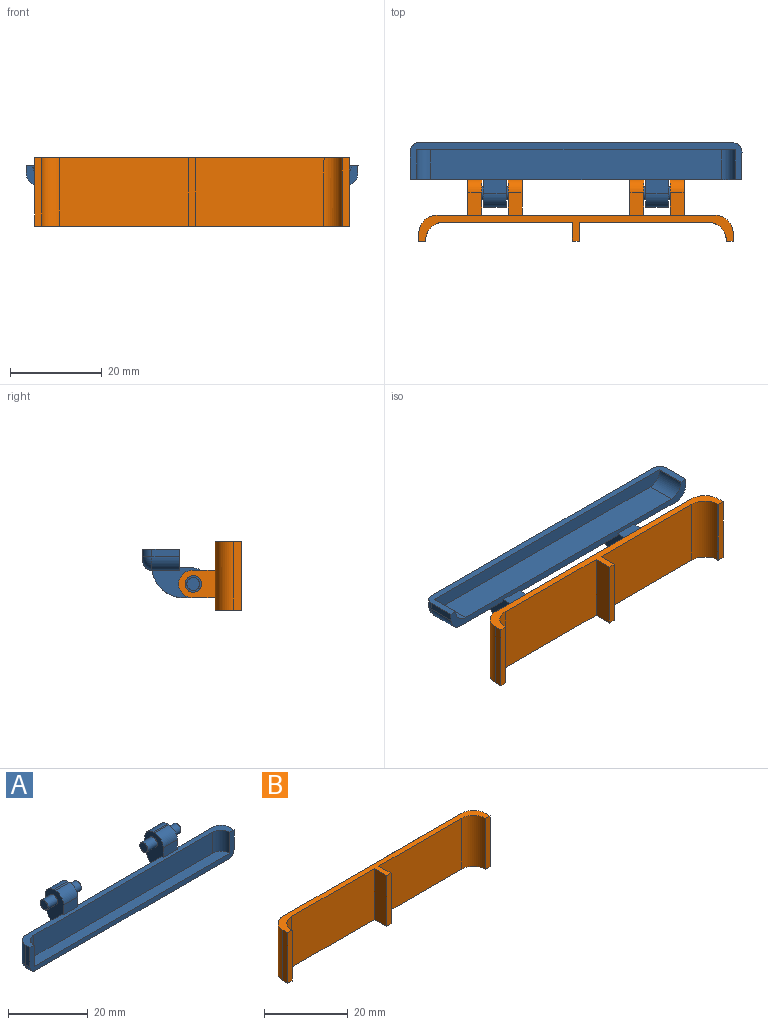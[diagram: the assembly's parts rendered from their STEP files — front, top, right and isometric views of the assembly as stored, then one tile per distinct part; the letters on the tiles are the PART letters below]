
ASSEMBLY  parts=2 mates=1
PART A: 45 faces, bbox 72.3x10.6x14 mm
  f0: plane 72.3x4.58mm, normal (0,0,1), area 112.7mm2, adj f2,f3,f4,f5,f9,f10,f11,f12
  f1: plane 68.3x2.58mm, normal (0,0,-1), area 175.9mm2, adj f7,f8,f17,f18,f19,f44
  f2: plane 6x1.58mm, normal (-1,0,0), area 9.5mm2, adj f0,f8,f12,f44
  f3: plane 6x1.58mm, normal (1,0,0), area 9.5mm2, adj f0,f7,f13,f44
  f4: plane 6.5x0.08mm, normal (-1,0,0), area 0.5mm2, adj f0,f6,f14,f44
  f5: plane 6.5x0.08mm, normal (1,0,0), area 0.5mm2, adj f0,f6,f16,f44
  f6: plane 69.3x3.08mm, normal (0,0,1), area 209.7mm2, adj f4,f5,f14,f15,f16,f44
  f7: cylinder r=2mm len=2mm, axis (0,-1,0), area 5mm2, adj f1,f3,f17,f44
  f8: cylinder r=2mm len=2mm, axis (0,1,0), area 5mm2, adj f1,f2,f18,f44
  f9: plane 13x6mm, normal (0,1,0), area 78mm2, adj f0,f13,f19,f26
  f10: plane 30.3x6mm, normal (0,1,0), area 181.8mm2, adj f0,f19,f22,f28
  f11: plane 13x6mm, normal (0,1,0), area 78mm2, adj f0,f12,f19,f20
  f12: cylinder r=3mm len=6mm, axis (0,0,1), area 28.3mm2, adj f0,f2,f11,f18
  f13: cylinder r=3mm len=6mm, axis (0,0,1), area 28.3mm2, adj f0,f3,f9,f17
  f14: cylinder r=3mm len=6.5mm, axis (0,0,1), area 30.6mm2, adj f0,f4,f6,f15
  f15: plane 63.3x6.5mm, normal (0,-1,0), area 411.4mm2, adj f0,f6,f14,f16
  f16: cylinder r=3mm len=6.5mm, axis (0,0,1), area 30.6mm2, adj f0,f5,f6,f15
  f17: torus R=1mm, axis (0,0,1), area 11.2mm2, adj f1,f7,f13,f19
  f18: torus R=1mm, axis (0,0,1), area 11.2mm2, adj f1,f8,f12,f19
  f19: cylinder r=2mm len=66.3mm, axis (1,0,0), area 208.3mm2, adj f1,f9,f10,f11,f17,f18,f42,f43
  f20: plane 12x6.5mm, normal (-1,0,0), area 54.9mm2, adj f0,f11,f21,f23,f24,f32,f33,f34
  f21: plane 5x3mm, normal (0,-1,0), area 15mm2, adj f0,f20,f22,f33
  f22: plane 12x6.5mm, normal (1,0,0), area 54.9mm2, adj f0,f10,f21,f23,f24,f32,f33,f36
  f23: plane 5x2.07mm, normal (0,1,0), area 10.4mm2, adj f20,f22,f32,f43
  f24: plane 5x0.5mm, normal (0,0,1), area 2.5mm2, adj f20,f22,f32,f33
  f25: plane 5x3mm, normal (0,-1,0), area 15mm2, adj f0,f26,f28,f31
  f26: plane 12x6.5mm, normal (1,0,0), area 54.9mm2, adj f0,f9,f25,f27,f29,f30,f31,f38
  f27: plane 5x2.07mm, normal (0,1,0), area 10.4mm2, adj f26,f28,f30,f42
  f28: plane 12x6.5mm, normal (-1,0,0), area 54.9mm2, adj f0,f10,f25,f27,f29,f30,f31,f40
  f29: plane 5x0.5mm, normal (0,0,1), area 2.5mm2, adj f26,f28,f30,f31
  f30: cylinder r=3mm len=5mm, axis (1,0,0), area 23.6mm2, adj f26,f27,f28,f29
  f31: cylinder r=3mm len=5mm, axis (-1,0,0), area 23.6mm2, adj f25,f26,f28,f29
  f32: cylinder r=3mm len=5mm, axis (1,0,0), area 23.6mm2, adj f20,f22,f23,f24
  f33: cylinder r=3mm len=5mm, axis (-1,0,0), area 23.6mm2, adj f20,f21,f22,f24
  f34: cylinder r=1.4mm len=3.4mm, axis (1,0,0), area 29.9mm2, adj f20,f35
  f35: plane 2.8x2.8mm, normal (-1,0,0), area 6.2mm2, adj f34
  f36: cylinder r=1.4mm len=3.4mm, axis (-1,0,0), area 29.9mm2, adj f22,f37
  f37: plane 2.8x2.8mm, normal (1,0,0), area 6.2mm2, adj f36
  f38: cylinder r=1.4mm len=3.4mm, axis (-1,0,0), area 29.9mm2, adj f26,f39
  f39: plane 2.8x2.8mm, normal (1,0,0), area 6.2mm2, adj f38
  f40: cylinder r=1.4mm len=3.4mm, axis (1,0,0), area 29.9mm2, adj f28,f41
  f41: plane 2.8x2.8mm, normal (-1,0,0), area 6.2mm2, adj f40
  f42: cylinder r=7mm len=6.93mm, axis (1,0,0), area 50mm2, adj f19,f26,f27,f28
  f43: cylinder r=7mm len=6.93mm, axis (1,0,0), area 50mm2, adj f19,f20,f22,f23
  f44: plane 72.3x8mm, normal (0,-1,0), area 126.2mm2, adj f0,f1,f2,f3,f4,f5,f6,f7
PART B: 42 faces, bbox 68.5x13.6x14.9 mm
  f0: plane 14.89x1.5mm, normal (0,-1,0), area 22.3mm2, adj f2,f3,f6,f41
  f1: plane 14.89x1.5mm, normal (0,-1,0), area 22.3mm2, adj f2,f7,f8,f41
  f2: plane 68.5x5.62mm, normal (0,0,1), area 121.3mm2, adj f0,f1,f3,f4,f5,f6,f7,f8
  f3: plane 14.89x1.62mm, normal (1,0,0), area 24.1mm2, adj f0,f2,f15,f41
  f4: plane 14.89x1.62mm, normal (-1,0,0), area 24.1mm2, adj f2,f14,f40,f41
  f5: plane 14.89x0.12mm, normal (1,0,0), area 1.8mm2, adj f2,f13,f40,f41
  f6: plane 14.89x0.12mm, normal (-1,0,0), area 1.8mm2, adj f0,f2,f12,f41
  f7: plane 14.89x4.12mm, normal (1,0,0), area 61.4mm2, adj f1,f2,f10,f41
  f8: plane 14.89x4.12mm, normal (-1,0,0), area 61.4mm2, adj f1,f2,f11,f41
  f9: plane 60.5x14.89mm, normal (0,1,0), area 828.5mm2, adj f2,f14,f15,f16,f17,f18,f19,f20
  f10: plane 28x14.89mm, normal (0,-1,0), area 416.8mm2, adj f2,f7,f12,f41
  f11: plane 28x14.89mm, normal (0,-1,0), area 416.8mm2, adj f2,f8,f13,f41
  f12: cylinder r=4mm len=14.89mm, axis (0,0,-1), area 93.5mm2, adj f2,f6,f10,f41
  f13: cylinder r=4mm len=14.89mm, axis (0,0,1), area 93.5mm2, adj f2,f5,f11,f41
  f14: cylinder r=4mm len=14.89mm, axis (0,0,-1), area 93.5mm2, adj f2,f4,f9,f41
  f15: cylinder r=4mm len=14.89mm, axis (0,0,1), area 93.5mm2, adj f2,f3,f9,f41
  f16: plane 8x6mm, normal (-1,0,0), area 34mm2, adj f9,f18,f19,f35,f39
  f17: plane 8x6mm, normal (1,0,0), area 34mm2, adj f9,f18,f19,f35,f39
  f18: plane 5x3mm, normal (0,0,-1), area 15mm2, adj f9,f16,f17,f39
  f19: plane 5x3mm, normal (0,0,1), area 15mm2, adj f9,f16,f17,f39
  f20: plane 8x6mm, normal (-1,0,0), area 34mm2, adj f9,f22,f23,f34,f38
  f21: plane 8x6mm, normal (1,0,0), area 34mm2, adj f9,f22,f23,f34,f38
  f22: plane 5x3mm, normal (0,0,-1), area 15mm2, adj f9,f20,f21,f38
  f23: plane 5x3mm, normal (0,0,1), area 15mm2, adj f9,f20,f21,f38
  f24: plane 8x6mm, normal (-1,0,0), area 34mm2, adj f9,f26,f27,f33,f37
  f25: plane 8x6mm, normal (1,0,0), area 34mm2, adj f9,f26,f27,f33,f37
  f26: plane 5x3mm, normal (0,0,-1), area 15mm2, adj f9,f24,f25,f37
  f27: plane 5x3mm, normal (0,0,1), area 15mm2, adj f9,f24,f25,f37
  f28: plane 8x6mm, normal (-1,0,0), area 34mm2, adj f9,f30,f31,f32,f36
  f29: plane 8x6mm, normal (1,0,0), area 34mm2, adj f9,f30,f31,f32,f36
  f30: plane 5x3mm, normal (0,0,-1), area 15mm2, adj f9,f28,f29,f36
  f31: plane 5x3mm, normal (0,0,1), area 15mm2, adj f9,f28,f29,f36
  f32: cylinder r=1.8mm len=3.6mm, axis (1,0,0), area 33.9mm2, adj f28,f29
  f33: cylinder r=1.8mm len=3.6mm, axis (1,0,0), area 33.9mm2, adj f24,f25
  f34: cylinder r=1.8mm len=3.6mm, axis (1,0,0), area 33.9mm2, adj f20,f21
  f35: cylinder r=1.8mm len=3.6mm, axis (1,0,0), area 33.9mm2, adj f16,f17
  f36: cylinder r=3mm len=6mm, axis (1,0,0), area 28.3mm2, adj f28,f29,f30,f31
  f37: cylinder r=3mm len=6mm, axis (1,0,0), area 28.3mm2, adj f24,f25,f26,f27
  f38: cylinder r=3mm len=6mm, axis (1,0,0), area 28.3mm2, adj f20,f21,f22,f23
  f39: cylinder r=3mm len=6mm, axis (1,0,0), area 28.3mm2, adj f16,f17,f18,f19
  f40: plane 14.89x1.5mm, normal (0,-1,0), area 22.3mm2, adj f2,f4,f5,f41
  f41: plane 68.5x5.62mm, normal (0,0,-1), area 121.3mm2, adj f0,f1,f3,f4,f5,f6,f7,f8
PLACE A rot(axis=(0,-0.71,0.71),180deg) t=(-39.9,-98.4,-62.82)mm
PLACE B rot(axis=(-0.18,0.89,-0.42),0deg) t=(-39.94,-138.45,-90.76)mm
MATE revolute A.f30 <-> B.f32  axis (1,0,0) through (-16.38,-101.41,-99.98)mm
